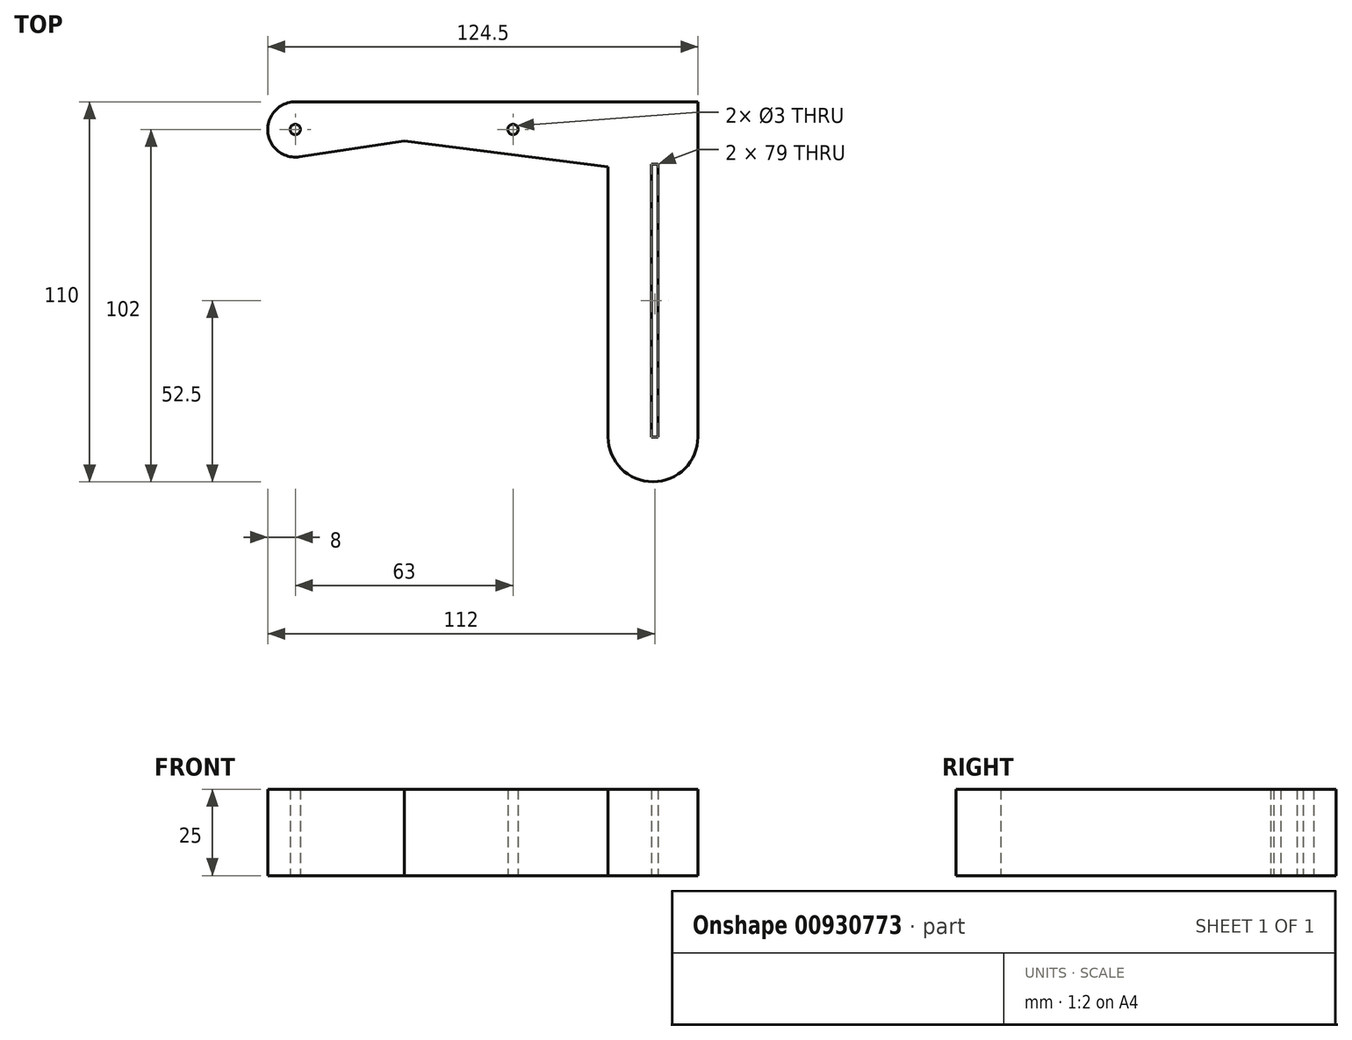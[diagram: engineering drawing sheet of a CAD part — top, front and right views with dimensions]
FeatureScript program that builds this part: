
annotation { "Feature Type Name" : "Feature", "Feature Type Description" : "" }
export const myFeature = defineFeature(function(context is Context, id is Id, definition is map)
    precondition{}
    {
        {
            var Q0;
            Q0=qCreatedBy(makeId("Top.planeOp"),FACE);
            var sketch = newSketch(context, id + "F0", { "sketchPlane" : qUnion([Q0])});
            skLineSegment(sketch, "E0", {"start": v(0, 0) * mm, "end": v(63, 0) * mm, "construction": true});
            skArc(sketch, "E1", {"start": v(0, 8) * mm, "mid": v(-7.98, -0.6) * mm, "end": v(1.19, -7.91) * mm});
            skLineSegment(sketch, "E2", {"start": v(0, 8) * mm, "end": v(116.5, 8) * mm});
            skLineSegment(sketch, "E3", {"start": v(31.5, 8) * mm, "end": v(31.5, -10.23) * mm, "construction": true});
            skLineSegment(sketch, "E4", {"start": v(31.5, -3.35) * mm, "end": v(1.19, -7.91) * mm});
            skLineSegment(sketch, "E5", {"start": v(31.5, -3.35) * mm, "end": v(90.5, -10.87) * mm});
            skLineSegment(sketch, "E6", {"start": v(116.5, 8) * mm, "end": v(116.5, -89) * mm});
            skLineSegment(sketch, "E7", {"start": v(103.5, -102) * mm, "end": v(103.5, -102) * mm});
            skLineSegment(sketch, "E8", {"start": v(90.5, -89) * mm, "end": v(90.5, -10.87) * mm});
            skPoint(sketch, "E9.orphan", {"position": v(63, 8) * mm});
            skPoint(sketch, "E10.visualSharp", {"position": v(116.5, -102) * mm});
            skArc(sketch, "E10.filletArc", {"start": v(103.5, -102) * mm, "mid": v(112.7, -98.2) * mm, "end": v(116.5, -89) * mm});
            skPoint(sketch, "E11.visualSharp", {"position": v(90.5, -102) * mm});
            skArc(sketch, "E11.filletArc", {"start": v(90.5, -89) * mm, "mid": v(94.3, -98.2) * mm, "end": v(103.5, -102) * mm});
            skCircle(sketch, "E12", {"center": v(0, 0) * mm, "radius": 1.5 * mm});
            skCircle(sketch, "E13", {"center": v(63, 0) * mm, "radius": 1.5 * mm});
            skLineSegment(sketch, "E14.0", {"start": v(105, -89) * mm, "end": v(105, -10) * mm});
            skLineSegment(sketch, "E15.0", {"start": v(103, -89) * mm, "end": v(103, -10) * mm});
            skLineSegment(sketch, "E16", {"start": v(103, -10) * mm, "end": v(105, -10) * mm});
            skLineSegment(sketch, "E17", {"start": v(103, -89) * mm, "end": v(105, -89) * mm});
            skSolve(sketch);
        }
        {
            var Q0;
            Q0=makeQuery(id+"F0.imprint","IMPRINT",FACE,{"disambiguationData":[TD([[makeQuery(id+"F0.imprint","IMPRINT",EDGE,{"derivedFrom":sQuery(id+"F0.wireOp",EDGE,"E1")}),1.0]])]});
            extrude(context, id + "F1", {"entities" : qUnion([Q0]), "depth" : 25 * mm, "offsetDistance" : 25 * mm});
        }
    });
